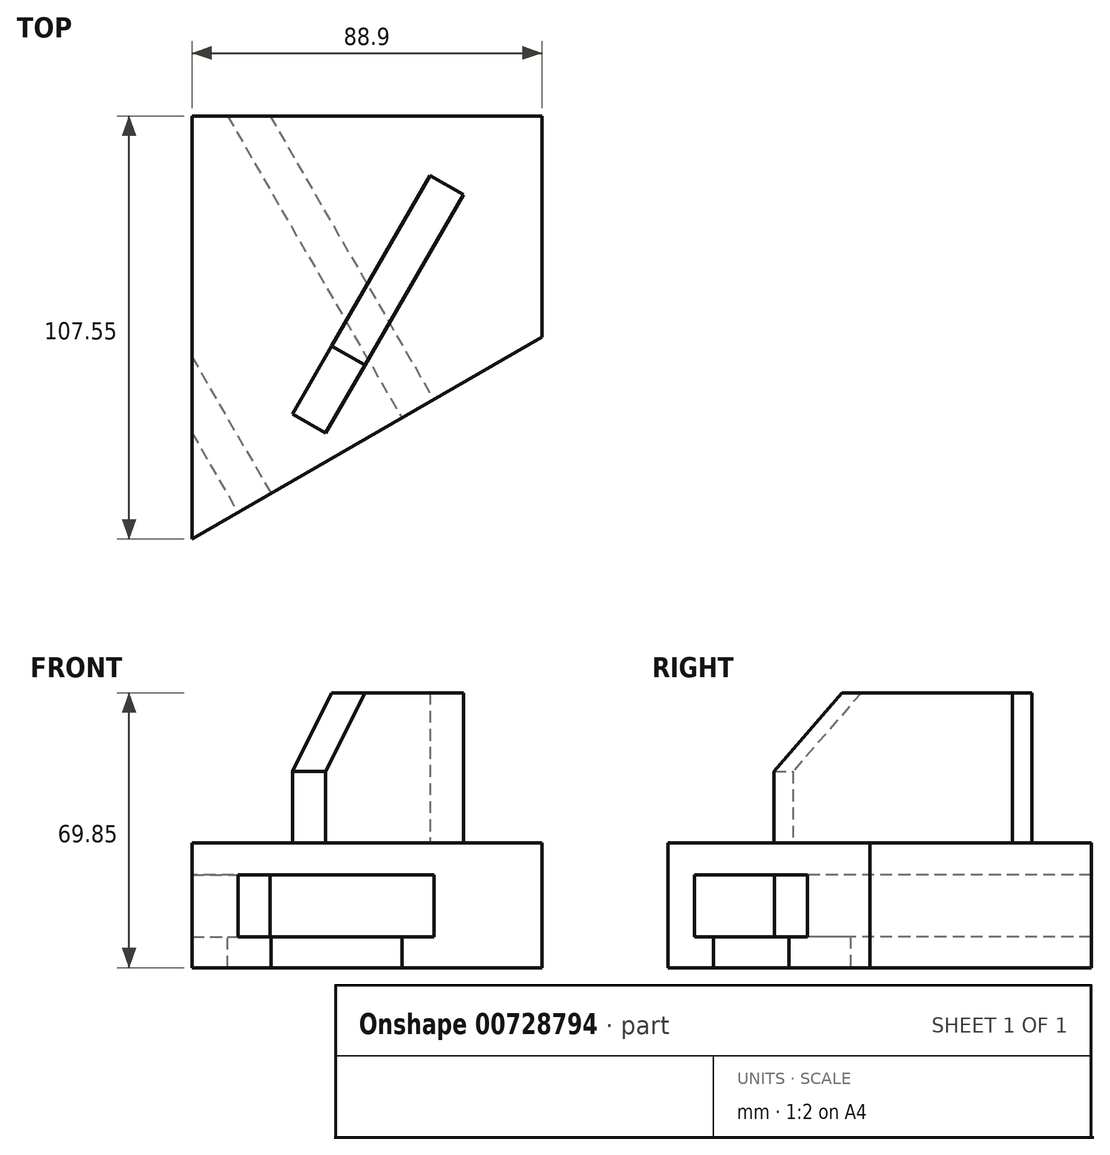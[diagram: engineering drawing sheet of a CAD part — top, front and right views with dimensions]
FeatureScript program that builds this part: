
annotation { "Feature Type Name" : "Feature", "Feature Type Description" : "" }
export const myFeature = defineFeature(function(context is Context, id is Id, definition is map)
    precondition{}
    {
        {
            var Q0;
            Q0=qCreatedBy(makeId("Top.planeOp"),FACE);
            var sketch = newSketch(context, id + "F0", { "sketchPlane" : qUnion([Q0])});
            skLineSegment(sketch, "E0", {"start": v(0, 107.55) * mm, "end": v(0, 0) * mm});
            skLineSegment(sketch, "E1", {"start": v(0, 0) * mm, "end": v(88.9, 51.33) * mm});
            skLineSegment(sketch, "E2", {"start": v(88.9, 51.33) * mm, "end": v(88.9, 107.55) * mm});
            skLineSegment(sketch, "E3", {"start": v(88.9, 107.55) * mm, "end": v(0, 107.55) * mm});
            skSolve(sketch);
        }
        {
            var Q0;
            Q0=makeQuery(id+"F0.imprint","IMPRINT",FACE,{"disambiguationData":[TD([[makeQuery(id+"F0.imprint","IMPRINT",EDGE,{"derivedFrom":sQuery(id+"F0.wireOp",EDGE,"E0")}),1.0]])]});
            extrude(context, id + "F1", {"entities" : qUnion([Q0]), "depth" : 31.75 * mm, "offsetDistance" : 25.4 * mm});
        }
        {
            var Q0;
            Q0=makeQuery(id+"F1.opExtrude","SWEPT_FACE",FACE,{"disambiguationData":[OSD([sQuery(id+"F0.wireOp",EDGE,"E1")])]});
            var sketch = newSketch(context, id + "F2", { "sketchPlane" : qUnion([Q0])});
            skLineSegment(sketch, "E4", {"start": v(13.5, 23.62) * mm, "end": v(13.5, 7.87) * mm});
            skLineSegment(sketch, "E5", {"start": v(13.5, 7.87) * mm, "end": v(13.5, 7.87) * mm});
            skLineSegment(sketch, "E6", {"start": v(23.15, 7.87) * mm, "end": v(13.5, 7.87) * mm});
            skLineSegment(sketch, "E7", {"start": v(23.15, 7.87) * mm, "end": v(23.15, 0) * mm});
            skLineSegment(sketch, "E8", {"start": v(70.9, 23.62) * mm, "end": v(13.5, 23.62) * mm});
            skLineSegment(sketch, "E9", {"start": v(70.9, 7.87) * mm, "end": v(70.9, 23.62) * mm});
            skLineSegment(sketch, "E10", {"start": v(61.55, 7.87) * mm, "end": v(70.9, 7.87) * mm});
            skLineSegment(sketch, "E11", {"start": v(61.55, 0) * mm, "end": v(61.55, 7.87) * mm});
            skLineSegment(sketch, "E12", {"start": v(23.15, 0) * mm, "end": v(61.55, 0) * mm});
            skSolve(sketch);
        }
        {
            var Q0;
            Q0=makeQuery(id+"F2.imprint","IMPRINT",FACE,{"disambiguationData":[TD([[makeQuery(id+"F2.imprint","IMPRINT",EDGE,{"derivedFrom":sQuery(id+"F2.wireOp",EDGE,"E4")}),1.0]])]});
            extrude(context, id + "F3", {"entities" : qUnion([Q0]), "operationType" : NewBodyOperationType.REMOVE, "oppositeDirection" : true, "depth" : 120 * mm, "hasOffset" : true, "offsetDistance" : 50 * mm});
        }
        {
            var Q0;
            Q0=makeQuery(id+"F1.opExtrude","CAP_FACE",FACE,{"disambiguationData":[OSD([sQuery(id+"F0.wireOp",EDGE,"E0"),sQuery(id+"F0.wireOp",EDGE,"E1"),sQuery(id+"F0.wireOp",EDGE,"E2"),sQuery(id+"F0.wireOp",EDGE,"E3")])],"isStart":false});
            var sketch = newSketch(context, id + "F4", { "sketchPlane" : qUnion([Q0])});
            skLineSegment(sketch, "E13", {"start": v(68.9, 87.55) * mm, "end": v(33.9, 26.93) * mm});
            skLineSegment(sketch, "E14", {"start": v(33.9, 26.93) * mm, "end": v(25.46, 31.8) * mm});
            skLineSegment(sketch, "E15", {"start": v(25.46, 31.8) * mm, "end": v(60.46, 92.42) * mm});
            skLineSegment(sketch, "E16", {"start": v(60.46, 92.42) * mm, "end": v(68.9, 87.55) * mm});
            skSolve(sketch);
        }
        {
            var Q0;
            Q0 = qSketchRegion(id + "F4", true);
            extrude(context, id + "F5", {"entities" : qUnion([Q0]), "operationType" : NewBodyOperationType.ADD, "depth" : 38.1 * mm, "offsetDistance" : 25 * mm});
        }
        {
            var Q0;
            Q0=makeQuery(id+"F5.opExtrude","CAP_EDGE",EDGE,{"disambiguationData":[OSD([sQuery(id+"F4.wireOp",EDGE,"E14")])],"isStart":false});
            chamfer(context, id + "F6", {"entities" : qUnion([Q0]), "width" : 20 * mm, "tangentPropagation" : true});
        }
    });
